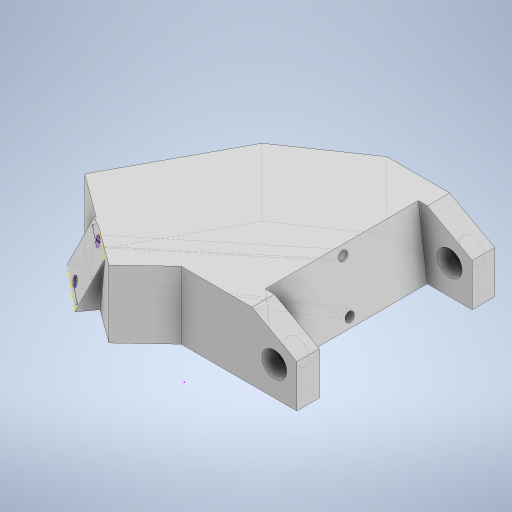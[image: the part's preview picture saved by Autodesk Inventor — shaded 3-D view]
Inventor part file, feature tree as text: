
AUTODESK INVENTOR PART (.ipt)
format: ipt  version: 2024 (Build 280153000, 153)  size: 899,584 bytes
history: native  units: mm
features: sketch x65, extrude x51, move_body x9, plane x6, split x6, boolean_combine x4, chamfer x3, loft x2, delete_face x1
ambient origin geometry x8: Origin, YZ Plane, XZ Plane, XY Plane, X Axis, Y Axis, Z Axis, Center Point
bodies: Solid1 (feature_tree), Solid2 (feature_tree), Solid3 (feature_tree), Solid4 (feature_tree), Solid5 (feature_tree), Solid6 (feature_tree), Solid7 (feature_tree), Solid8 (feature_tree), Solid9 (feature_tree), Solid10 (feature_tree), Solid11 (feature_tree), Solid12 (feature_tree), Solid13 (feature_tree)
feature tree (147):
  extrude  "Extrusion1"  Depth=16.0mm
  sketch  "Sketch2"  dims[d2=15.0mm d3=0.0mm d4=10.0mm]
  extrude  "Extrusion2"  Depth=10.0mm
  chamfer  "Chamfer1"  Distance=21.25mm
  extrude  "Extrusion3"  Depth=10.0mm TaperAngle=0.0deg
  extrude  "Extrusion4"  Depth=11.5mm TaperAngle=0.0deg
  extrude  "Extrusion5"  Depth=1.0mm TaperAngle=0.0deg
  chamfer  "Chamfer2"  Distance=6.0mm Angle=45.0deg
  sketch  "Sketch6"  dims[d14=7.0mm d15=11.5mm d16=0.0mm]
  extrude  "Extrusion6"  Depth=9.0mm
  extrude  "Extrusion7"  Depth=45.25mm TaperAngle=0.0deg
  chamfer  "Chamfer3"  Distance=11.5mm Angle=45.0deg
  sketch  "Sketch9"  dims[d26=3.3mm d27=45.25mm d28=0.0mm d29=11.5mm d30=5.5mm d31=45.0deg]
  extrude  "Extrusion8"  Depth=2.0mm TaperAngle=0.0deg
  extrude  "Extrusion9"  Depth=9.0mm TaperAngle=0.0deg
  extrude  "Extrusion10"  Depth=13.0mm TaperAngle=0.0deg
  sketch  "Sketch13"  dims[d43=24.0mm d44=21.0mm d45=0.0mm]
  extrude  "Extrusion11"  Depth=21.0mm TaperAngle=0.0deg
  extrude  "Extrusion12"  TaperAngle=0.0deg  [1 undecoded]
  extrude  "Extrusion13"  Depth=1.0mm
  plane  "Work Plane1"
  split  "Split1"
  move_body  "Move Body1"
  extrude  "Extrusion14"  Depth=1.0mm TaperAngle=0.0deg
  delete_face  "Delete Face1"
  extrude  "Extrusion17"  Depth=1.0mm
  extrude  "Extrusion18"  Depth=1.2mm TaperAngle=0.0deg
  extrude  "Extrusion19"  [1 undecoded]
  extrude  "Extrusion20"  Depth=1.75mm
  plane  "Work Plane2"
  split  "Split2"
  move_body  "Move Body2"
  boolean_combine  "Combine1"
  plane  "Work Plane3"
  split  "Split3"
  move_body  "Move Body3"
  boolean_combine  "Combine2"
  split  "Split4"
  split  "Split5"
  move_body  "Move Body4"
  move_body  "Move Body5"
  extrude  "Extrusion22"  Depth=20.0mm TaperAngle=0.0deg
  extrude  "Extrusion23"  Depth=12.0mm
  move_body  "Move Body6"
  move_body  "Move Body7"
  boolean_combine  "Combine3"
  extrude  "Extrusion24"  Depth=12.0mm TaperAngle=0.0deg
  plane  "Work Plane5"
  sketch  "Sketch32"  dims[d110=8.0mm d111=0.0mm d112=5.5mm]
  plane  "Work Plane6"
  extrude  "Extrusion27"  Depth=8.0mm TaperAngle=0.0deg
  plane  "Work Plane4"
  extrude  "Extrusion28"  Depth=123.0mm TaperAngle=0.0deg
  sketch  "Sketch35"  dims[d121=2.0mm d122=0.0mm d123=8.0mm d124=0.0mm]
  extrude  "Extrusion29"  Depth=82.0mm TaperAngle=0.0deg
  extrude  "Extrusion30"  Depth=5.5mm
  extrude  "Extrusion31"  Depth=40.0mm TaperAngle=0.0deg
  sketch  "Sketch38"  dims[d131=15.0mm d132=0.0mm d133=15.0mm d134=0.0mm]
  extrude  "Extrusion32"  Depth=2.0mm TaperAngle=0.0deg
  extrude  "Extrusion33"  Depth=2.0mm TaperAngle=0.0deg
  extrude  "Extrusion34"  Depth=25.394541mm
  extrude  "Extrusion35"  Depth=15.0mm TaperAngle=0.0deg
  extrude  "Extrusion36"  Depth=15.0mm TaperAngle=0.0deg
  extrude  "Extrusion37"  Depth=15.0mm TaperAngle=0.0deg
  extrude  "Extrusion38"  Depth=15.0mm TaperAngle=0.0deg
  extrude  "Extrusion39"  Depth=6.75mm TaperAngle=0.0deg
  extrude  "Extrusion40"  Depth=10.0mm
  extrude  "Extrusion41"  Depth=2.0mm TaperAngle=0.0deg
  extrude  "Extrusion42"  Depth=9.0mm
  extrude  "Extrusion43"  Depth=20.5mm TaperAngle=0.0deg
  extrude  "Extrusion44"  Depth=22.0mm TaperAngle=0.0deg
  split  "Split6"
  move_body  "Move Body8"
  extrude  "Extrusion45"  Depth=10.0mm
  move_body  "Move Body9"
  boolean_combine  "Combine4"
  extrude  "Extrusion46"  Depth=13.706mm
  extrude  "Extrusion47"  Depth=2.0mm
  sketch  "Sketch56"  dims[d224=0.0mm d225=90.0deg d226=0.0mm d227=90.0deg]
  extrude  "Extrusion48"  Depth=2.0mm TaperAngle=0.0deg
  extrude  "Extrusion49"  Depth=3.75mm
  extrude  "Extrusion50"  TaperAngle=90.0deg  [1 undecoded]
  extrude  "Extrusion51"  Depth=2.0mm
  extrude  "Extrusion52"  TaperAngle=0.0deg  [1 undecoded]
  sketch  "Sketch67"  dims[d247=6.75mm d248=0.0mm]
  extrude  "Extrusion53"  Depth=2.0mm
  loft  "Loft3"
  loft  "Loft4"
  sketch  "Sketch73"  dims[d241=0.872665mm]
  sketch  "Sketch74"  dims[d249=0.5mm]
  extrude  "Extrusion55"  Depth=2.0mm
  extrude  "Extrusion56"  Depth=2.0mm
  extrude  "Extrusion57"  Depth=34.0mm TaperAngle=0.0deg
  sketch  "Sketch1"  dims[d0=36.0mm d1=16.0mm]
  sketch  "Sketch3"  dims[d5=10.0mm]
  sketch  "Sketch4"  dims[d6=3.3mm d7=21.25mm d8=0.0mm]
  sketch  "Sketch5"  dims[d9=10.0mm d10=5.5mm d11=45.0deg d12=10.0mm d13=0.0mm]
  sketch  "Sketch7"  dims[d17=3.3mm d18=1.0mm d19=0.0mm d20=6.0mm d21=11.5mm d22=45.0deg]
  sketch  "Sketch8"  dims[d23=15.0mm d24=0.0mm d25=9.0mm]
  sketch  "Sketch10"  dims[d32=2.0mm d33=65.75mm d34=0.0mm]
  sketch  "Sketch11"  dims[d35=0.5mm d36=0.0mm d37=9.0mm d38=0.0mm]
  sketch  "Sketch12"  dims[d39=0.5mm d40=0.0mm d41=13.0mm d42=0.0mm]
  sketch  "Sketch14"  dims[d46=12.25mm d47=-12.0mm d48=0.0mm d49=0.0mm]
  sketch  "Sketch15"  dims[d50=10.0mm d51=0.0mm d61=1.0mm]
  sketch  "Sketch16"  dims[d62=1.0mm d63=1.5mm d64=0.0mm]
  sketch  "Sketch17"  dims[d65=1.0mm d66=1.0mm]
  sketch  "Sketch20"  dims[d67=5.5mm d68=0.0mm d69=1.2mm d70=0.0mm]
  sketch  "Sketch21"  dims[d71=2.2mm d72=0.0mm d73=-5.5mm]
  sketch  "Sketch22"  dims[d74=-3.0mm d75=0.0mm d76=0.0mm d79=1.75mm]
  sketch  "Sketch23"  dims[d80=3.0mm d81=0.0mm d82=0.0mm d83=0.0mm d84=0.0mm d85=20.0mm]
  sketch  "Sketch25"  dims[d86=0.0mm d87=0.0mm d88=-20.0mm d89=12.0mm]
  sketch  "Sketch26"  dims[d90=12.0mm d91=0.0mm d92=12.0mm d93=0.0mm]
  sketch  "Sketch27"  dims[d94=0.0mm d95=0.0mm d96=-8.0mm d97=0.0mm d98=0.0mm d99=8.0mm]
  sketch  "Sketch28"  dims[d100=4.5mm d101=123.0mm d102=0.0mm]
  sketch  "Sketch29"  dims[d107=5.1mm d108=82.0mm d109=0.0mm]
  sketch  "Sketch33"  dims[d113=40.0mm d114=0.0mm d115=40.0mm d116=0.0mm]
  sketch  "Sketch34"  dims[d117=40.0mm d118=0.0mm d119=2.0mm d120=0.0mm]
  sketch  "Sketch36"  dims[d125=20.0mm d126=25.394541mm]
  sketch  "Sketch37"  dims[d127=15.0mm d128=0.0mm d129=15.0mm d130=0.0mm]
  sketch  "Sketch39"  dims[d135=15.0mm d136=0.0mm d137=15.0mm d138=0.0mm]
  sketch  "Sketch40"  dims[d139=6.3338mm d140=15.0mm d141=0.0mm]
  sketch  "Sketch41"  dims[d142=15.0mm d143=0.0mm d144=6.75mm d145=0.0mm]
  sketch  "Sketch42"  dims[d146=30.0mm d147=0.0mm d148=10.0mm]
  sketch  "Sketch43"  dims[d149=-5.0mm d150=0.0mm d151=0.0mm d152=2.0mm d153=0.0mm]
  sketch  "Sketch44"  dims[d154=3.0mm d155=0.0mm d156=0.0mm d157=9.0mm]
  sketch  "Sketch45"  dims[d158=5.0mm d159=0.0mm d160=20.5mm d161=0.0mm]
  sketch  "Sketch46"  dims[d166=20.5mm d167=0.0mm d174=22.0mm d175=0.0mm]
  sketch  "Sketch47"  dims[d189=10.0mm d190=0.0mm d191=9.0mm]
  sketch  "Sketch48"  dims[d192=27.925268mm d193=13.706mm]
  sketch  "Sketch49"  dims[d194=2.0mm d195=1.95mm]
  sketch  "Sketch50"  dims[d197=2.0mm d198=4.0mm d199=0.0mm]
  sketch  "Sketch51"  dims[d200=11.25mm d201=0.0mm d202=3.75mm d203=2.792527mm]
  sketch  "Sketch52"  dims[d204=2.0mm d205=90.0deg]
  sketch  "Sketch53"  dims[d207=2.0mm d212=2.0mm]
  sketch  "Sketch54"  dims[d214=0.0mm d215=90.0deg d216=0.0mm d217=90.0deg]
  sketch  "Sketch55"  dims[d220=2.0mm d223=2.0mm]
  sketch  "Sketch59"  dims[d231=2.0mm d232=2.0mm]
  sketch  "Sketch64"  dims[d233=34.0mm d238=2.0mm]
  sketch  "Sketch65"  dims[d239=2.0mm d242=2.0mm]
  sketch  "Sketch66"  dims[d243=34.0mm d244=0.0mm d245=34.0mm d246=0.0mm]
  sketch  "Sketch68"  dims[d52=0.5mm]
  sketch  "Sketch69"  dims[d53=0.872665mm]
  sketch  "Sketch70"  dims[d103=0.5mm]
  sketch  "Sketch71"  dims[d104=0.872665mm]
  sketch  "Sketch72"  dims[d240=0.5mm]
  sketch  "Sketch75"  dims[d250=0.872665mm]
  sketch  "Sketch76"
note: 4 required parameter values undecoded (feature->parameter linkage not recoverable at this tier; creation-order binding heuristic only, values carry confidence <= 0.55)
